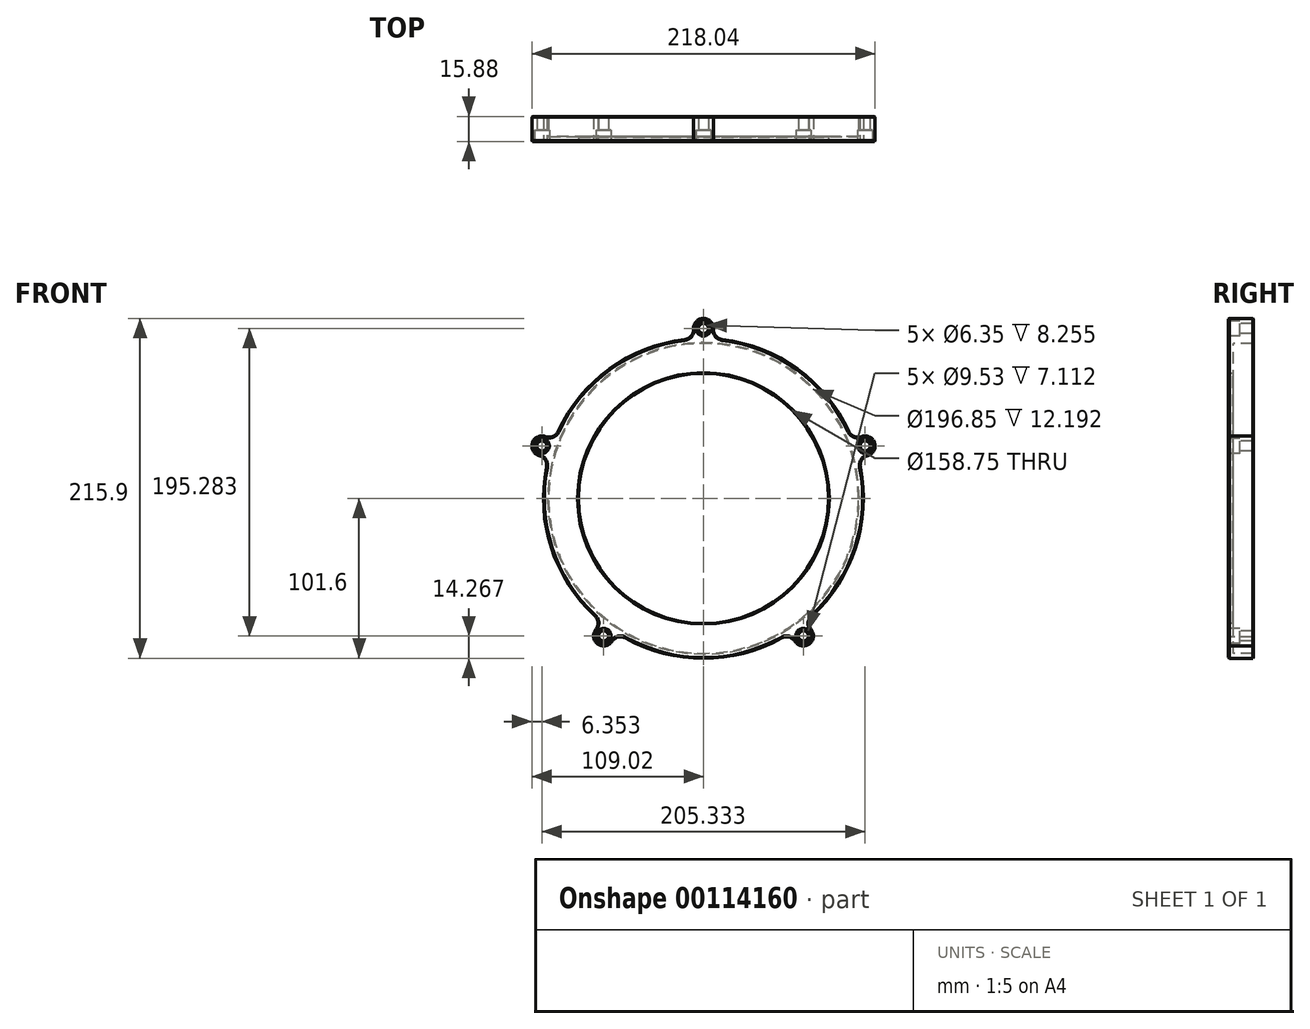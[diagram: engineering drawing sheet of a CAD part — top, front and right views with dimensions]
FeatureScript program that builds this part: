
annotation { "Feature Type Name" : "Feature", "Feature Type Description" : "" }
export const myFeature = defineFeature(function(context is Context, id is Id, definition is map)
    precondition{}
    {
        {
            var Q0;
            Q0=qCreatedBy(makeId("Front.planeOp"),FACE);
            var sketch = newSketch(context, id + "F0", { "sketchPlane" : qUnion([Q0])});
            skCircle(sketch, "E0", {"center": v(0, 0) * mm, "radius": 101.6 * mm});
            skCircle(sketch, "E1", {"center": v(0, 0) * mm, "radius": 79.38 * mm});
            skCircle(sketch, "E2", {"center": v(0, 107.95) * mm, "radius": 6.35 * mm});
            skCircle(sketch, "E3", {"center": v(0, 0) * mm, "radius": 98.43 * mm});
            skLineSegment(sketch, "E4", {"start": v(6.35, 107.95) * mm, "end": v(6.35, 101.4) * mm});
            skLineSegment(sketch, "E5", {"start": v(-6.35, 107.95) * mm, "end": v(-6.35, 101.4) * mm});
            skCircle(sketch, "E6", {"center": v(0, 107.95) * mm, "radius": 3.18 * mm});
            skLineSegment(sketch, "E7.1.0", {"start": v(-104.63, 27.32) * mm, "end": v(-98.4, 25.3) * mm});
            skCircle(sketch, "E7.1.1", {"center": v(-102.67, 33.36) * mm, "radius": 3.18 * mm});
            skLineSegment(sketch, "E7.1.2", {"start": v(-100.7, 39.4) * mm, "end": v(-94.48, 37.37) * mm});
            skCircle(sketch, "E7.1.3", {"center": v(-102.67, 33.36) * mm, "radius": 6.35 * mm});
            skLineSegment(sketch, "E7.2.0", {"start": v(-58.31, -91.07) * mm, "end": v(-54.46, -85.77) * mm});
            skCircle(sketch, "E7.2.1", {"center": v(-63.45, -87.33) * mm, "radius": 3.18 * mm});
            skLineSegment(sketch, "E7.2.2", {"start": v(-68.59, -83.6) * mm, "end": v(-64.74, -78.3) * mm});
            skCircle(sketch, "E7.2.3", {"center": v(-63.45, -87.33) * mm, "radius": 6.35 * mm});
            skLineSegment(sketch, "E8.2.3.0", {"start": v(68.59, -83.6) * mm, "end": v(64.74, -78.3) * mm});
            skCircle(sketch, "E8.3.3.0", {"center": v(63.45, -87.33) * mm, "radius": 3.18 * mm});
            skLineSegment(sketch, "E8.5.3.0", {"start": v(58.31, -91.07) * mm, "end": v(54.46, -85.77) * mm});
            skCircle(sketch, "E8.8.3.0", {"center": v(63.45, -87.33) * mm, "radius": 6.35 * mm});
            skLineSegment(sketch, "E9.2.4.0", {"start": v(100.7, 39.4) * mm, "end": v(94.48, 37.37) * mm});
            skCircle(sketch, "E9.3.4.0", {"center": v(102.67, 33.36) * mm, "radius": 3.18 * mm});
            skLineSegment(sketch, "E9.5.4.0", {"start": v(104.63, 27.32) * mm, "end": v(98.4, 25.3) * mm});
            skCircle(sketch, "E9.8.4.0", {"center": v(102.67, 33.36) * mm, "radius": 6.35 * mm});
            skSolve(sketch);
        }
        {
            var Q0;
            {var subQ0=sQuery(id+"F0.wireOp",EDGE,"E9.2.4.0");Q0=makeQuery(id+"F0.imprint","IMPRINT",FACE,{"disambiguationData":[TD([[makeQuery(id+"F0.imprint","IMPRINT",EDGE,{"derivedFrom":subQ0}),1.0]])]});}
            var Q1;
            {var subQ0=sQuery(id+"F0.wireOp",EDGE,"E9.5.4.0");Q1=makeQuery(id+"F0.imprint","IMPRINT",FACE,{"disambiguationData":[TD([[makeQuery(id+"F0.imprint","IMPRINT",EDGE,{"derivedFrom":subQ0}),-1.0]])]});}
            var Q2;
            Q2=makeQuery(id+"F0.imprint","IMPRINT",FACE,{"disambiguationData":[TD([[makeQuery(id+"F0.imprint","IMPRINT",EDGE,{"derivedFrom":sQuery(id+"F0.wireOp",EDGE,"E9.3.4.0")}),-1.0]])]});
            var Q3;
            {var subQ0=sQuery(id+"F0.wireOp",EDGE,"E8.2.3.0");Q3=makeQuery(id+"F0.imprint","IMPRINT",FACE,{"disambiguationData":[TD([[makeQuery(id+"F0.imprint","IMPRINT",EDGE,{"derivedFrom":subQ0}),1.0]])]});}
            var Q4;
            Q4=makeQuery(id+"F0.imprint","IMPRINT",FACE,{"disambiguationData":[TD([[makeQuery(id+"F0.imprint","IMPRINT",EDGE,{"derivedFrom":sQuery(id+"F0.wireOp",EDGE,"E8.3.3.0")}),-1.0]])]});
            var Q5;
            {var subQ0=sQuery(id+"F0.wireOp",EDGE,"E8.5.3.0");Q5=makeQuery(id+"F0.imprint","IMPRINT",FACE,{"disambiguationData":[TD([[makeQuery(id+"F0.imprint","IMPRINT",EDGE,{"derivedFrom":subQ0}),-1.0]])]});}
            var Q6;
            {var subQ0=sQuery(id+"F0.wireOp",EDGE,"E7.2.0");Q6=makeQuery(id+"F0.imprint","IMPRINT",FACE,{"disambiguationData":[TD([[makeQuery(id+"F0.imprint","IMPRINT",EDGE,{"derivedFrom":subQ0}),1.0]])]});}
            var Q7;
            {var subQ0=sQuery(id+"F0.wireOp",EDGE,"E7.2.2");Q7=makeQuery(id+"F0.imprint","IMPRINT",FACE,{"disambiguationData":[TD([[makeQuery(id+"F0.imprint","IMPRINT",EDGE,{"derivedFrom":subQ0}),-1.0]])]});}
            var Q8;
            Q8=makeQuery(id+"F0.imprint","IMPRINT",FACE,{"disambiguationData":[TD([[makeQuery(id+"F0.imprint","IMPRINT",EDGE,{"derivedFrom":sQuery(id+"F0.wireOp",EDGE,"E7.2.1")}),-1.0]])]});
            var Q9;
            Q9=makeQuery(id+"F0.imprint","IMPRINT",FACE,{"disambiguationData":[TD([[makeQuery(id+"F0.imprint","IMPRINT",EDGE,{"derivedFrom":sQuery(id+"F0.wireOp",EDGE,"E7.1.1")}),-1.0]])]});
            var Q10;
            {var subQ0=sQuery(id+"F0.wireOp",EDGE,"E7.1.2");Q10=makeQuery(id+"F0.imprint","IMPRINT",FACE,{"disambiguationData":[TD([[makeQuery(id+"F0.imprint","IMPRINT",EDGE,{"derivedFrom":subQ0}),-1.0]])]});}
            var Q11;
            {var subQ0=sQuery(id+"F0.wireOp",EDGE,"E7.1.0");Q11=makeQuery(id+"F0.imprint","IMPRINT",FACE,{"disambiguationData":[TD([[makeQuery(id+"F0.imprint","IMPRINT",EDGE,{"derivedFrom":subQ0}),1.0]])]});}
            var Q12;
            Q12=makeQuery(id+"F0.imprint","IMPRINT",FACE,{"disambiguationData":[TD([[makeQuery(id+"F0.imprint","IMPRINT",EDGE,{"derivedFrom":sQuery(id+"F0.wireOp",EDGE,"E6")}),-1.0]])]});
            var Q13;
            {var subQ0=sQuery(id+"F0.wireOp",EDGE,"E4");Q13=makeQuery(id+"F0.imprint","IMPRINT",FACE,{"disambiguationData":[TD([[makeQuery(id+"F0.imprint","IMPRINT",EDGE,{"derivedFrom":subQ0}),-1.0]])]});}
            var Q14;
            {var subQ0=sQuery(id+"F0.wireOp",EDGE,"E5");Q14=makeQuery(id+"F0.imprint","IMPRINT",FACE,{"disambiguationData":[TD([[makeQuery(id+"F0.imprint","IMPRINT",EDGE,{"derivedFrom":subQ0}),1.0]])]});}
            var Q15;
            Q15=makeQuery(id+"F0.imprint","IMPRINT",FACE,{"disambiguationData":[TD([[makeQuery(id+"F0.imprint","IMPRINT",EDGE,{"derivedFrom":sQuery(id+"F0.wireOp",EDGE,"E3")}),-1.0]])]});
            extrude(context, id + "F1", {"entities" : qUnion([Q0, Q1, Q2, Q3, Q4, Q5, Q6, Q7, Q8, Q9, Q10, Q11, Q12, Q13, Q14, Q15]), "oppositeDirection" : true, "depth" : 15.88 * mm});
        }
        {
            var Q0;
            Q0=makeQuery(id+"F0.imprint","IMPRINT",FACE,{"disambiguationData":[TD([[makeQuery(id+"F0.imprint","IMPRINT",EDGE,{"derivedFrom":sQuery(id+"F0.wireOp",EDGE,"E1")}),-1.0]])]});
            extrude(context, id + "F2", {"entities" : qUnion([Q0]), "operationType" : NewBodyOperationType.ADD, "oppositeDirection" : true, "depth" : 3.17 * mm});
        }
        {
            var Q0;
            Q0=makeQuery(id+"F1.opExtrude","SWEPT_EDGE",EDGE,{"disambiguationData":[OSD([sQuery(id+"F0.wireOp",EDGE,"E0"),sQuery(id+"F0.wireOp",EDGE,"E7.1.0")])]});
            var Q1;
            Q1=makeQuery(id+"F1.opExtrude","SWEPT_EDGE",EDGE,{"disambiguationData":[OSD([sQuery(id+"F0.wireOp",EDGE,"E0"),sQuery(id+"F0.wireOp",EDGE,"E7.2.2")])]});
            var Q2;
            Q2=makeQuery(id+"F1.opExtrude","SWEPT_EDGE",EDGE,{"disambiguationData":[OSD([sQuery(id+"F0.wireOp",EDGE,"E0"),sQuery(id+"F0.wireOp",EDGE,"E7.2.0")])]});
            var Q3;
            Q3=makeQuery(id+"F1.opExtrude","SWEPT_EDGE",EDGE,{"disambiguationData":[OSD([sQuery(id+"F0.wireOp",EDGE,"E0"),sQuery(id+"F0.wireOp",EDGE,"E8.5.3.0")])]});
            var Q4;
            Q4=makeQuery(id+"F1.opExtrude","SWEPT_EDGE",EDGE,{"disambiguationData":[OSD([sQuery(id+"F0.wireOp",EDGE,"E0"),sQuery(id+"F0.wireOp",EDGE,"E8.2.3.0")])]});
            var Q5;
            Q5=makeQuery(id+"F1.opExtrude","SWEPT_EDGE",EDGE,{"disambiguationData":[OSD([sQuery(id+"F0.wireOp",EDGE,"E0"),sQuery(id+"F0.wireOp",EDGE,"E9.2.4.0")])]});
            var Q6;
            Q6=makeQuery(id+"F1.opExtrude","SWEPT_EDGE",EDGE,{"disambiguationData":[OSD([sQuery(id+"F0.wireOp",EDGE,"E0"),sQuery(id+"F0.wireOp",EDGE,"E4")])]});
            var Q7;
            Q7=makeQuery(id+"F1.opExtrude","SWEPT_EDGE",EDGE,{"disambiguationData":[OSD([sQuery(id+"F0.wireOp",EDGE,"E0"),sQuery(id+"F0.wireOp",EDGE,"E5")])]});
            var Q8;
            Q8=makeQuery(id+"F1.opExtrude","SWEPT_EDGE",EDGE,{"disambiguationData":[OSD([sQuery(id+"F0.wireOp",EDGE,"E0"),sQuery(id+"F0.wireOp",EDGE,"E7.1.2")])]});
            var Q9;
            Q9=makeQuery(id+"F1.opExtrude","SWEPT_EDGE",EDGE,{"disambiguationData":[OSD([sQuery(id+"F0.wireOp",EDGE,"E0"),sQuery(id+"F0.wireOp",EDGE,"E9.5.4.0")])]});
            fillet(context, id + "F3", {"entities" : qUnion([Q0, Q1, Q2, Q3, Q4, Q5, Q6, Q7, Q8, Q9]), "radius" : 6.35 * mm, "tangentPropagation" : true, "allowEdgeOverflow" : false});
        }
        {
            var Q0;
            {var subQ0=sQuery(id+"F0.wireOp",EDGE,"E3");Q0=makeQuery(id+"F2.boolean.opBoolean","MERGE",FACE,{"derivedFrom":[makeQuery(id+"F1.opExtrude","CAP_FACE",FACE,{"disambiguationData":[OSD([sQuery(id+"F0.wireOp",EDGE,"E0"),sQuery(id+"F0.wireOp",EDGE,"E2"),subQ0,sQuery(id+"F0.wireOp",EDGE,"E4"),sQuery(id+"F0.wireOp",EDGE,"E5"),sQuery(id+"F0.wireOp",EDGE,"E6"),sQuery(id+"F0.wireOp",EDGE,"E7.1.0"),sQuery(id+"F0.wireOp",EDGE,"E7.1.1"),sQuery(id+"F0.wireOp",EDGE,"E7.1.2"),sQuery(id+"F0.wireOp",EDGE,"E7.1.3"),sQuery(id+"F0.wireOp",EDGE,"E7.2.0"),sQuery(id+"F0.wireOp",EDGE,"E7.2.1"),sQuery(id+"F0.wireOp",EDGE,"E7.2.2"),sQuery(id+"F0.wireOp",EDGE,"E7.2.3"),sQuery(id+"F0.wireOp",EDGE,"E8.2.3.0"),sQuery(id+"F0.wireOp",EDGE,"E8.3.3.0"),sQuery(id+"F0.wireOp",EDGE,"E8.5.3.0"),sQuery(id+"F0.wireOp",EDGE,"E8.8.3.0"),sQuery(id+"F0.wireOp",EDGE,"E9.2.4.0"),sQuery(id+"F0.wireOp",EDGE,"E9.3.4.0"),sQuery(id+"F0.wireOp",EDGE,"E9.5.4.0"),sQuery(id+"F0.wireOp",EDGE,"E9.8.4.0")])],"isStart":true}),makeQuery(id+"F2.opExtrude","CAP_FACE",FACE,{"disambiguationData":[OSD([sQuery(id+"F0.wireOp",EDGE,"E1"),subQ0])],"isStart":true})]});}
            var sketch = newSketch(context, id + "F4", { "sketchPlane" : qUnion([Q0])});
            skCircle(sketch, "E10", {"center": v(0, 107.95) * mm, "radius": 4.76 * mm});
            skCircle(sketch, "E11.1.0", {"center": v(-102.67, 33.36) * mm, "radius": 4.76 * mm});
            skCircle(sketch, "E11.2.0", {"center": v(-63.45, -87.33) * mm, "radius": 4.76 * mm});
            skCircle(sketch, "E11.3.0", {"center": v(63.45, -87.33) * mm, "radius": 4.76 * mm});
            skCircle(sketch, "E11.4.0", {"center": v(102.67, 33.36) * mm, "radius": 4.76 * mm});
            skPoint(sketch, "E11.center", {"position": v(0, 0) * mm});
            skSolve(sketch);
        }
        {
            var Q0;
            Q0=makeQuery(id+"F4.imprint","IMPRINT",FACE,{"disambiguationData":[TD([[makeQuery(id+"F4.imprint","IMPRINT",EDGE,{"derivedFrom":sQuery(id+"F4.wireOp",EDGE,"E11.2.0")}),1.0]])]});
            var Q1;
            Q1=makeQuery(id+"F4.imprint","IMPRINT",FACE,{"disambiguationData":[TD([[makeQuery(id+"F4.imprint","IMPRINT",EDGE,{"derivedFrom":sQuery(id+"F4.wireOp",EDGE,"E11.1.0")}),1.0]])]});
            var Q2;
            Q2=makeQuery(id+"F4.imprint","IMPRINT",FACE,{"disambiguationData":[TD([[makeQuery(id+"F4.imprint","IMPRINT",EDGE,{"derivedFrom":sQuery(id+"F4.wireOp",EDGE,"E10")}),1.0]])]});
            var Q3;
            Q3=makeQuery(id+"F4.imprint","IMPRINT",FACE,{"disambiguationData":[TD([[makeQuery(id+"F4.imprint","IMPRINT",EDGE,{"derivedFrom":sQuery(id+"F4.wireOp",EDGE,"E11.4.0")}),1.0]])]});
            var Q4;
            Q4=makeQuery(id+"F4.imprint","IMPRINT",FACE,{"disambiguationData":[TD([[makeQuery(id+"F4.imprint","IMPRINT",EDGE,{"derivedFrom":sQuery(id+"F4.wireOp",EDGE,"E11.3.0")}),1.0]])]});
            extrude(context, id + "F5", {"entities" : qUnion([Q0, Q1, Q2, Q3, Q4]), "operationType" : NewBodyOperationType.REMOVE, "oppositeDirection" : true, "depth" : 7.11 * mm});
        }
        {
            var Q0;
            {var subQ0=sQuery(id+"F0.wireOp",EDGE,"E0");Q0=makeQuery(id+"F1.opExtrude","CAP_EDGE",EDGE,{"disambiguationData":[OSD([subQ0]),TDD([makeQuery(id+"F0.imprint","IMPRINT",EDGE,{"disambiguationData":[TD([[makeQuery(id+"F0.imprint","INTERSECT",VERTEX,{"derivedFrom":[subQ0,sQuery(id+"F0.wireOp",EDGE,"E5")]}),-1.0]])],"derivedFrom":subQ0})])],"isStart":true});}
            var Q1;
            {var subQ0=sQuery(id+"F0.wireOp",EDGE,"E0");Q1=makeQuery(id+"F1.opExtrude","CAP_EDGE",EDGE,{"disambiguationData":[OSD([subQ0]),TDD([makeQuery(id+"F0.imprint","IMPRINT",EDGE,{"disambiguationData":[TD([[makeQuery(id+"F0.imprint","INTERSECT",VERTEX,{"derivedFrom":[subQ0,sQuery(id+"F0.wireOp",EDGE,"E7.1.0")]}),-1.0]])],"derivedFrom":subQ0})])],"isStart":false});}
            var Q2;
            Q2=makeQuery(id+"F2.opExtrude","CAP_EDGE",EDGE,{"disambiguationData":[OSD([sQuery(id+"F0.wireOp",EDGE,"E1")])],"isStart":false});
            var Q3;
            Q3=makeQuery(id+"F2.opExtrude","CAP_EDGE",EDGE,{"disambiguationData":[OSD([sQuery(id+"F0.wireOp",EDGE,"E1")])],"isStart":true});
            var Q4;
            Q4=makeQuery(id+"F5.boolean.opBoolean","COPY",EDGE,{"derivedFrom":makeQuery(id+"F5.opExtrude","CAP_EDGE",EDGE,{"disambiguationData":[OSD([sQuery(id+"F4.wireOp",EDGE,"E11.1.0")])],"isStart":true})});
            var Q5;
            Q5=makeQuery(id+"F5.boolean.opBoolean","COPY",EDGE,{"derivedFrom":makeQuery(id+"F5.opExtrude","CAP_EDGE",EDGE,{"disambiguationData":[OSD([sQuery(id+"F4.wireOp",EDGE,"E10")])],"isStart":true})});
            var Q6;
            Q6=makeQuery(id+"F5.boolean.opBoolean","COPY",EDGE,{"derivedFrom":makeQuery(id+"F5.opExtrude","CAP_EDGE",EDGE,{"disambiguationData":[OSD([sQuery(id+"F4.wireOp",EDGE,"E11.2.0")])],"isStart":true})});
            var Q7;
            Q7=makeQuery(id+"F5.boolean.opBoolean","COPY",EDGE,{"derivedFrom":makeQuery(id+"F5.opExtrude","CAP_EDGE",EDGE,{"disambiguationData":[OSD([sQuery(id+"F4.wireOp",EDGE,"E11.4.0")])],"isStart":true})});
            var Q8;
            Q8=makeQuery(id+"F5.boolean.opBoolean","COPY",EDGE,{"derivedFrom":makeQuery(id+"F5.opExtrude","CAP_EDGE",EDGE,{"disambiguationData":[OSD([sQuery(id+"F4.wireOp",EDGE,"E11.3.0")])],"isStart":true})});
            var Q9;
            Q9=makeQuery(id+"F1.opExtrude","CAP_EDGE",EDGE,{"disambiguationData":[OSD([sQuery(id+"F0.wireOp",EDGE,"E3")])],"isStart":false});
            var Q10;
            Q10=makeQuery(id+"F1.opExtrude","CAP_EDGE",EDGE,{"disambiguationData":[OSD([sQuery(id+"F0.wireOp",EDGE,"E6")])],"isStart":false});
            var Q11;
            Q11=makeQuery(id+"F1.opExtrude","CAP_EDGE",EDGE,{"disambiguationData":[OSD([sQuery(id+"F0.wireOp",EDGE,"E7.1.1")])],"isStart":false});
            var Q12;
            Q12=makeQuery(id+"F1.opExtrude","CAP_EDGE",EDGE,{"disambiguationData":[OSD([sQuery(id+"F0.wireOp",EDGE,"E7.2.1")])],"isStart":false});
            var Q13;
            Q13=makeQuery(id+"F1.opExtrude","CAP_EDGE",EDGE,{"disambiguationData":[OSD([sQuery(id+"F0.wireOp",EDGE,"E8.3.3.0")])],"isStart":false});
            var Q14;
            Q14=makeQuery(id+"F1.opExtrude","CAP_EDGE",EDGE,{"disambiguationData":[OSD([sQuery(id+"F0.wireOp",EDGE,"E9.3.4.0")])],"isStart":false});
            chamfer(context, id + "F6", {"entities" : qUnion([Q0, Q1, Q2, Q3, Q4, Q5, Q6, Q7, Q8, Q9, Q10, Q11, Q12, Q13, Q14]), "width" : 0.5 * mm, "tangentPropagation" : true});
        }
    });
